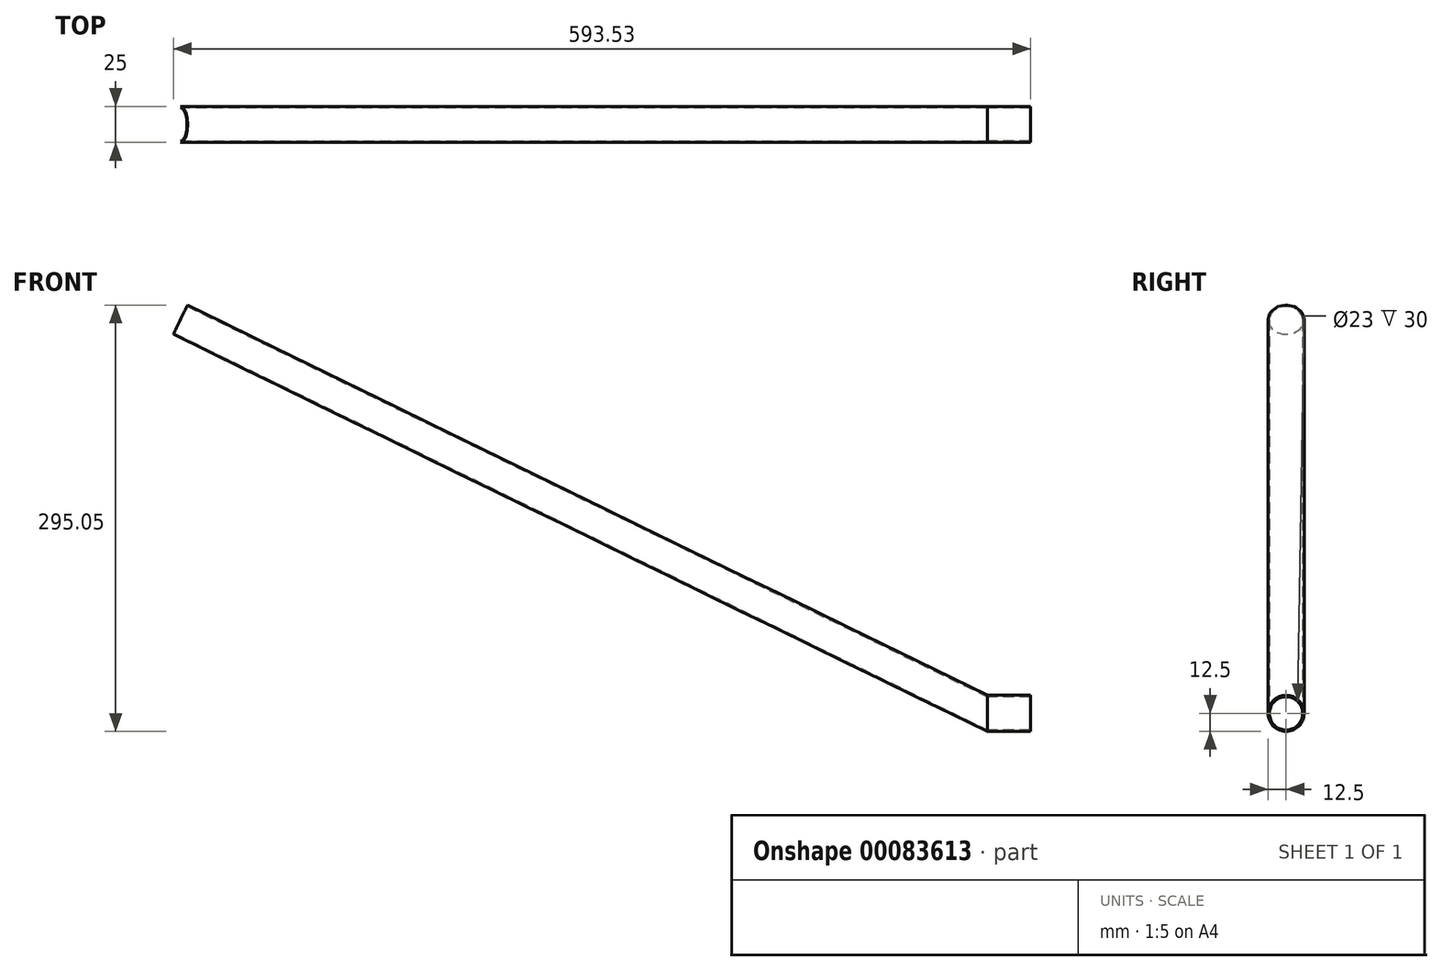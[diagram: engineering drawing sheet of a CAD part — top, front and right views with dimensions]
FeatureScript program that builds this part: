
annotation { "Feature Type Name" : "Feature", "Feature Type Description" : "" }
export const myFeature = defineFeature(function(context is Context, id is Id, definition is map)
    precondition{}
    {
        {
            var Q0;
            Q0=qCreatedBy(makeId("Right.planeOp"),FACE);
            var sketch = newSketch(context, id + "F0", { "sketchPlane" : qUnion([Q0])});
            skCircle(sketch, "E0", {"center": v(0, 0) * mm, "radius": 12.5 * mm});
            skCircle(sketch, "E1", {"center": v(0, 0) * mm, "radius": 11.5 * mm});
            skSolve(sketch);
        }
        {
            var Q0;
            Q0 = qSketchRegion(id + "F0", true);
            extrude(context, id + "F1", {"entities" : qUnion([Q0]), "depth" : 30 * mm});
        }
        {
            var Q0;
            Q0=qCreatedBy(makeId("Top.planeOp"),FACE);
            var sketch = newSketch(context, id + "F2", { "sketchPlane" : qUnion([Q0])});
            skLineSegment(sketch, "E2", {"start": v(0, 0) * mm, "end": v(0, -68.33) * mm, "construction": true});
            skSolve(sketch);
        }
        {
            var Q0;
            Q0=sQuery(id+"F2.wireOp",EDGE,"E2");
            cPlane(context, id + "F3", {"entities" : qUnion([Q0]), "cplaneType" : CPlaneType.LINE_ANGLE, "offset" : 150 * mm, "angle" : 64 * degree, "width" : 150 * mm, "height" : 150 * mm});
        }
        {
            var Q0;
            Q0=qCreatedBy(id+"F3.planeOp",FACE);
            cPlane(context, id + "F4", {"entities" : qUnion([Q0]), "cplaneType" : CPlaneType.OFFSET, "offset" : 621.5 * mm, "oppositeDirection" : true, "width" : 150 * mm, "height" : 150 * mm});
        }
        {
            var Q0;
            Q0=qCreatedBy(id+"F4.planeOp",FACE);
            var sketch = newSketch(context, id + "F5", { "sketchPlane" : qUnion([Q0])});
            skEllipse(sketch, "E3.0", {"center": v(0, 0) * mm, "majorRadius": 12.5 * mm, "minorRadius": 11.23 * mm, "majorAxis": v(1, 0)});
            skEllipse(sketch, "E4.0", {"center": v(0, 0) * mm, "majorRadius": 11.5 * mm, "minorRadius": 10.34 * mm, "majorAxis": v(1, 0)});
            skSolve(sketch);
        }
        {
            var Q0;
            Q0=makeQuery(id+"F5.imprint","IMPRINT",FACE,{"disambiguationData":[TD([[makeQuery(id+"F5.imprint","IMPRINT",EDGE,{"derivedFrom":sQuery(id+"F5.wireOp",EDGE,"E3.0")}),1.0]])]});
            var Q1;
            Q1=makeQuery(id+"F1.opExtrude","SWEPT_BODY",BODY,{"disambiguationData":[OSD([sQuery(id+"F0.wireOp",EDGE,"E0"),sQuery(id+"F0.wireOp",EDGE,"E1")])]});
            extrude(context, id + "F6", {"entities" : qUnion([Q0]), "operationType" : NewBodyOperationType.ADD, "endBound" : BoundingType.UP_TO_BODY, "endBoundEntityBody" : qUnion([Q1]), "depth" : 25 * mm});
        }
    });
